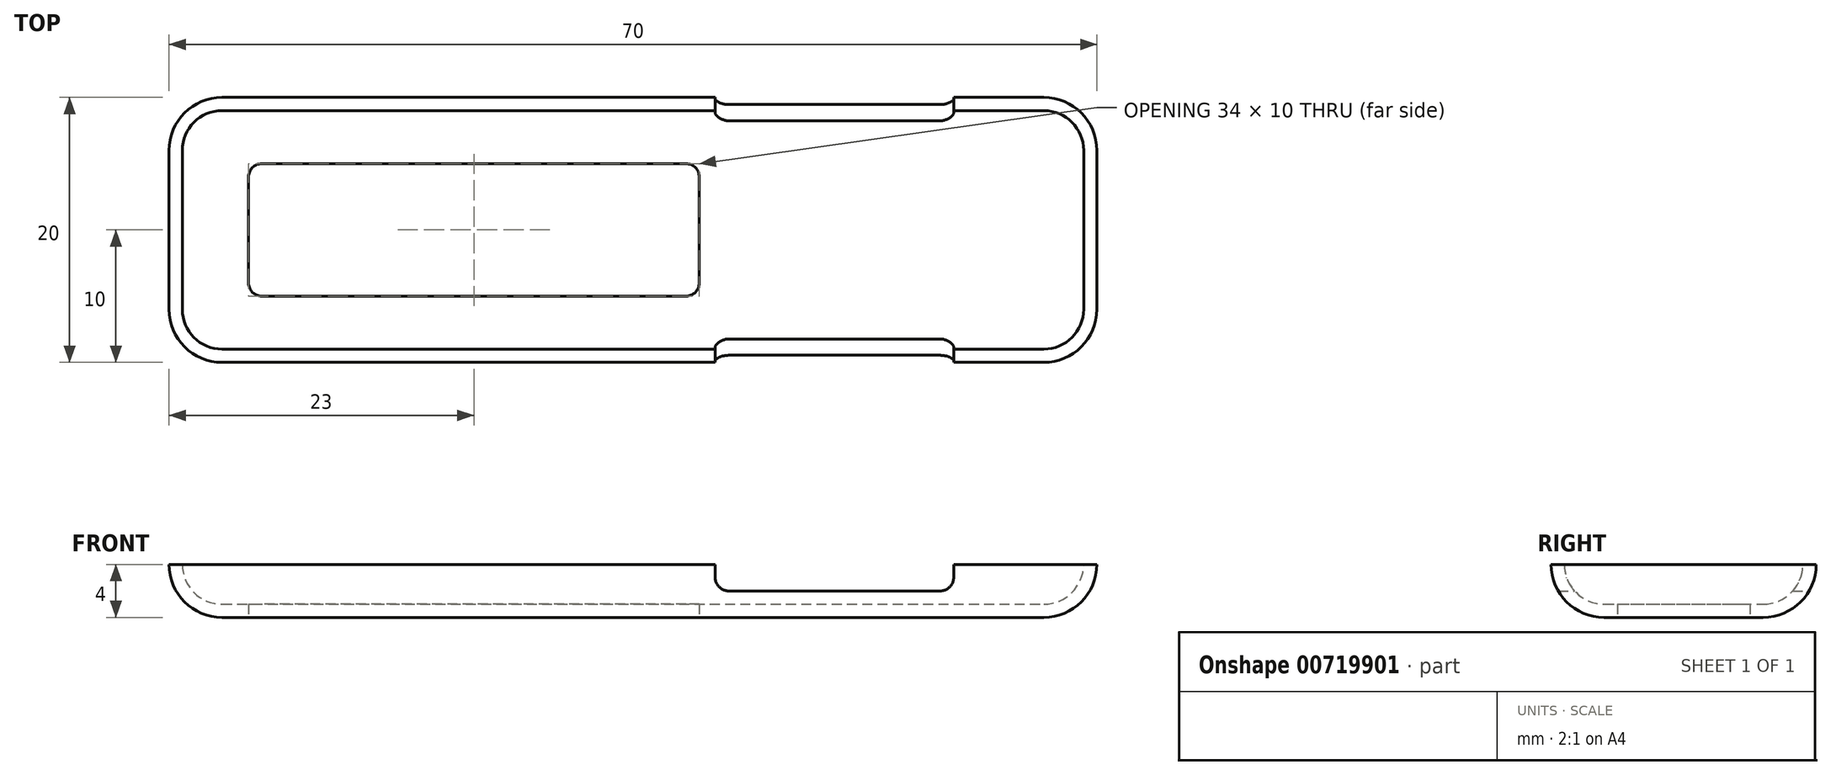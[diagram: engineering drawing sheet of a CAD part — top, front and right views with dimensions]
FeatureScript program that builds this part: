
annotation { "Feature Type Name" : "Feature", "Feature Type Description" : "" }
export const myFeature = defineFeature(function(context is Context, id is Id, definition is map)
    precondition{}
    {
        {
            var Q0;
            Q0=qCreatedBy(makeId("Top.planeOp"),FACE);
            var sketch = newSketch(context, id + "F0", { "sketchPlane" : qUnion([Q0])});
            skLineSegment(sketch, "E0.bottom", {"start": v(35, 10) * mm, "end": v(-35, 10) * mm});
            skLineSegment(sketch, "E0.top", {"start": v(35, -10) * mm, "end": v(-35, -10) * mm});
            skLineSegment(sketch, "E0.left", {"start": v(35, 10) * mm, "end": v(35, -10) * mm});
            skLineSegment(sketch, "E0.right", {"start": v(-35, 10) * mm, "end": v(-35, -10) * mm});
            skPoint(sketch, "E0.middle", {"position": v(0, 0) * mm});
            skSolve(sketch);
        }
        {
            var Q0;
            Q0=makeQuery(id+"F0.imprint","IMPRINT",FACE,{"disambiguationData":[TD([[makeQuery(id+"F0.imprint","IMPRINT",EDGE,{"derivedFrom":sQuery(id+"F0.wireOp",EDGE,"E0.bottom")}),1.0]])]});
            extrude(context, id + "F1", {"entities" : qUnion([Q0]), "depth" : 4 * mm, "offsetDistance" : 25 * mm});
        }
        {
            var Q0;
            Q0=makeQuery(id+"F1.opExtrude","CAP_FACE",FACE,{"disambiguationData":[OSD([sQuery(id+"F0.wireOp",EDGE,"E0.bottom"),sQuery(id+"F0.wireOp",EDGE,"E0.top"),sQuery(id+"F0.wireOp",EDGE,"E0.left"),sQuery(id+"F0.wireOp",EDGE,"E0.right")])],"isStart":true});
            var Q1;
            Q1=makeQuery(id+"F1.opExtrude","SWEPT_EDGE",EDGE,{"disambiguationData":[OSD([sQuery(id+"F0.wireOp",EDGE,"E0.top"),sQuery(id+"F0.wireOp",EDGE,"E0.right")])]});
            var Q2;
            Q2=makeQuery(id+"F1.opExtrude","SWEPT_EDGE",EDGE,{"disambiguationData":[OSD([sQuery(id+"F0.wireOp",EDGE,"E0.bottom"),sQuery(id+"F0.wireOp",EDGE,"E0.right")])]});
            var Q3;
            Q3=makeQuery(id+"F1.opExtrude","SWEPT_EDGE",EDGE,{"disambiguationData":[OSD([sQuery(id+"F0.wireOp",EDGE,"E0.bottom"),sQuery(id+"F0.wireOp",EDGE,"E0.left")])]});
            var Q4;
            Q4=makeQuery(id+"F1.opExtrude","SWEPT_EDGE",EDGE,{"disambiguationData":[OSD([sQuery(id+"F0.wireOp",EDGE,"E0.top"),sQuery(id+"F0.wireOp",EDGE,"E0.left")])]});
            fillet(context, id + "F2", {"entities" : qUnion([Q0, Q1, Q2, Q3, Q4]), "radius" : 4 * mm, "tangentPropagation" : true, "allowEdgeOverflow" : false});
        }
        {
            var Q0;
            Q0=makeQuery(id+"F1.opExtrude","CAP_FACE",FACE,{"disambiguationData":[OSD([sQuery(id+"F0.wireOp",EDGE,"E0.bottom"),sQuery(id+"F0.wireOp",EDGE,"E0.top"),sQuery(id+"F0.wireOp",EDGE,"E0.left"),sQuery(id+"F0.wireOp",EDGE,"E0.right")])],"isStart":false});
            shell(context, id + "F3", {"entities" : qUnion([Q0]), "thickness" : 1 * mm});
        }
        {
            var Q0;
            Q0=makeQuery(id+"F1.opExtrude","CAP_FACE",FACE,{"disambiguationData":[OSD([sQuery(id+"F0.wireOp",EDGE,"E0.bottom"),sQuery(id+"F0.wireOp",EDGE,"E0.top"),sQuery(id+"F0.wireOp",EDGE,"E0.left"),sQuery(id+"F0.wireOp",EDGE,"E0.right")])],"isStart":false});
            var sketch = newSketch(context, id + "F4", { "sketchPlane" : qUnion([Q0])});
            skLineSegment(sketch, "E1.bottom", {"start": v(6.2, -10) * mm, "end": v(24.2, -10) * mm});
            skLineSegment(sketch, "E1.top", {"start": v(6.2, 10) * mm, "end": v(24.2, 10) * mm});
            skLineSegment(sketch, "E1.left", {"start": v(6.2, -10) * mm, "end": v(6.2, 10) * mm});
            skLineSegment(sketch, "E1.right", {"start": v(24.2, -10) * mm, "end": v(24.2, 10) * mm});
            skPoint(sketch, "E1.middle", {"position": v(15.2, 0) * mm});
            skSolve(sketch);
        }
        {
            var Q0;
            Q0=qSketchRegion(id+"F4",true);
            extrude(context, id + "F5", {"entities" : qUnion([Q0]), "operationType" : NewBodyOperationType.REMOVE, "oppositeDirection" : true, "depth" : 2 * mm, "offsetDistance" : 25 * mm});
        }
        {
            var Q0;
            {var subQ0=sQuery(id+"F0.wireOp",EDGE,"E0.bottom");var subQ1=sQuery(id+"F4.wireOp",EDGE,"E1.right");Q0=makeQuery(id+"F5.boolean.opBoolean","COPY",EDGE,{"disambiguationData":[TD([makeQuery(id+"F2.opFillet","BLEND_FACE",FACE,{"disambiguationData":[OSD([subQ0])]})])],"derivedFrom":makeQuery(id+"F5.opExtrude","CAP_EDGE",EDGE,{"disambiguationData":[OSD([subQ1])],"isStart":false})});}
            var Q1;
            {var subQ0=sQuery(id+"F0.wireOp",EDGE,"E0.bottom");var subQ1=sQuery(id+"F4.wireOp",EDGE,"E1.left");Q1=makeQuery(id+"F5.boolean.opBoolean","COPY",EDGE,{"disambiguationData":[TD([makeQuery(id+"F2.opFillet","BLEND_FACE",FACE,{"disambiguationData":[OSD([subQ0])]})])],"derivedFrom":makeQuery(id+"F5.opExtrude","CAP_EDGE",EDGE,{"disambiguationData":[OSD([subQ1])],"isStart":false})});}
            var Q2;
            {var subQ0=sQuery(id+"F0.wireOp",EDGE,"E0.top");var subQ1=sQuery(id+"F4.wireOp",EDGE,"E1.left");Q2=makeQuery(id+"F5.boolean.opBoolean","COPY",EDGE,{"disambiguationData":[TD([makeQuery(id+"F2.opFillet","BLEND_FACE",FACE,{"disambiguationData":[OSD([subQ0])]})])],"derivedFrom":makeQuery(id+"F5.opExtrude","CAP_EDGE",EDGE,{"disambiguationData":[OSD([subQ1])],"isStart":false})});}
            var Q3;
            {var subQ0=sQuery(id+"F0.wireOp",EDGE,"E0.top");var subQ1=sQuery(id+"F4.wireOp",EDGE,"E1.right");Q3=makeQuery(id+"F5.boolean.opBoolean","COPY",EDGE,{"disambiguationData":[TD([makeQuery(id+"F2.opFillet","BLEND_FACE",FACE,{"disambiguationData":[OSD([subQ0])]})])],"derivedFrom":makeQuery(id+"F5.opExtrude","CAP_EDGE",EDGE,{"disambiguationData":[OSD([subQ1])],"isStart":false})});}
            fillet(context, id + "F6", {"entities" : qUnion([Q0, Q1, Q2, Q3]), "radius" : 1 * mm, "tangentPropagation" : true, "allowEdgeOverflow" : false});
        }
        {
            var Q0;
            Q0=makeQuery(id+"F1.opExtrude","CAP_FACE",FACE,{"disambiguationData":[OSD([sQuery(id+"F0.wireOp",EDGE,"E0.bottom"),sQuery(id+"F0.wireOp",EDGE,"E0.top"),sQuery(id+"F0.wireOp",EDGE,"E0.left"),sQuery(id+"F0.wireOp",EDGE,"E0.right")])],"isStart":true});
            var sketch = newSketch(context, id + "F7", { "sketchPlane" : qUnion([Q0])});
            skLineSegment(sketch, "E2.bottom", {"start": v(5, 5) * mm, "end": v(-29, 5) * mm});
            skLineSegment(sketch, "E2.top", {"start": v(5, -5) * mm, "end": v(-29, -5) * mm});
            skLineSegment(sketch, "E2.left", {"start": v(5, 5) * mm, "end": v(5, -5) * mm});
            skLineSegment(sketch, "E2.right", {"start": v(-29, 5) * mm, "end": v(-29, -5) * mm});
            skPoint(sketch, "E2.middle", {"position": v(-12, 0) * mm});
            skSolve(sketch);
        }
        {
            var Q0;
            Q0 = qSketchRegion(id + "F7", true);
            extrude(context, id + "F8", {"entities" : qUnion([Q0]), "operationType" : NewBodyOperationType.REMOVE, "endBound" : BoundingType.UP_TO_NEXT, "oppositeDirection" : true, "depth" : 25 * mm, "offsetDistance" : 25 * mm});
        }
        {
            var Q0;
            Q0=makeQuery(id+"F8.boolean.opBoolean","COPY",EDGE,{"derivedFrom":makeQuery(id+"F8.opExtrude","SWEPT_EDGE",EDGE,{"disambiguationData":[OSD([sQuery(id+"F7.wireOp",EDGE,"E2.bottom"),sQuery(id+"F7.wireOp",EDGE,"E2.left")])]})});
            var Q1;
            Q1=makeQuery(id+"F8.boolean.opBoolean","COPY",EDGE,{"derivedFrom":makeQuery(id+"F8.opExtrude","SWEPT_EDGE",EDGE,{"disambiguationData":[OSD([sQuery(id+"F7.wireOp",EDGE,"E2.top"),sQuery(id+"F7.wireOp",EDGE,"E2.left")])]})});
            var Q2;
            Q2=makeQuery(id+"F8.boolean.opBoolean","COPY",EDGE,{"derivedFrom":makeQuery(id+"F8.opExtrude","SWEPT_EDGE",EDGE,{"disambiguationData":[OSD([sQuery(id+"F7.wireOp",EDGE,"E2.top"),sQuery(id+"F7.wireOp",EDGE,"E2.right")])]})});
            var Q3;
            Q3=makeQuery(id+"F8.boolean.opBoolean","COPY",EDGE,{"derivedFrom":makeQuery(id+"F8.opExtrude","SWEPT_EDGE",EDGE,{"disambiguationData":[OSD([sQuery(id+"F7.wireOp",EDGE,"E2.bottom"),sQuery(id+"F7.wireOp",EDGE,"E2.right")])]})});
            fillet(context, id + "F9", {"entities" : qUnion([Q0, Q1, Q2, Q3]), "radius" : 1 * mm, "tangentPropagation" : true, "allowEdgeOverflow" : false});
        }
    });
